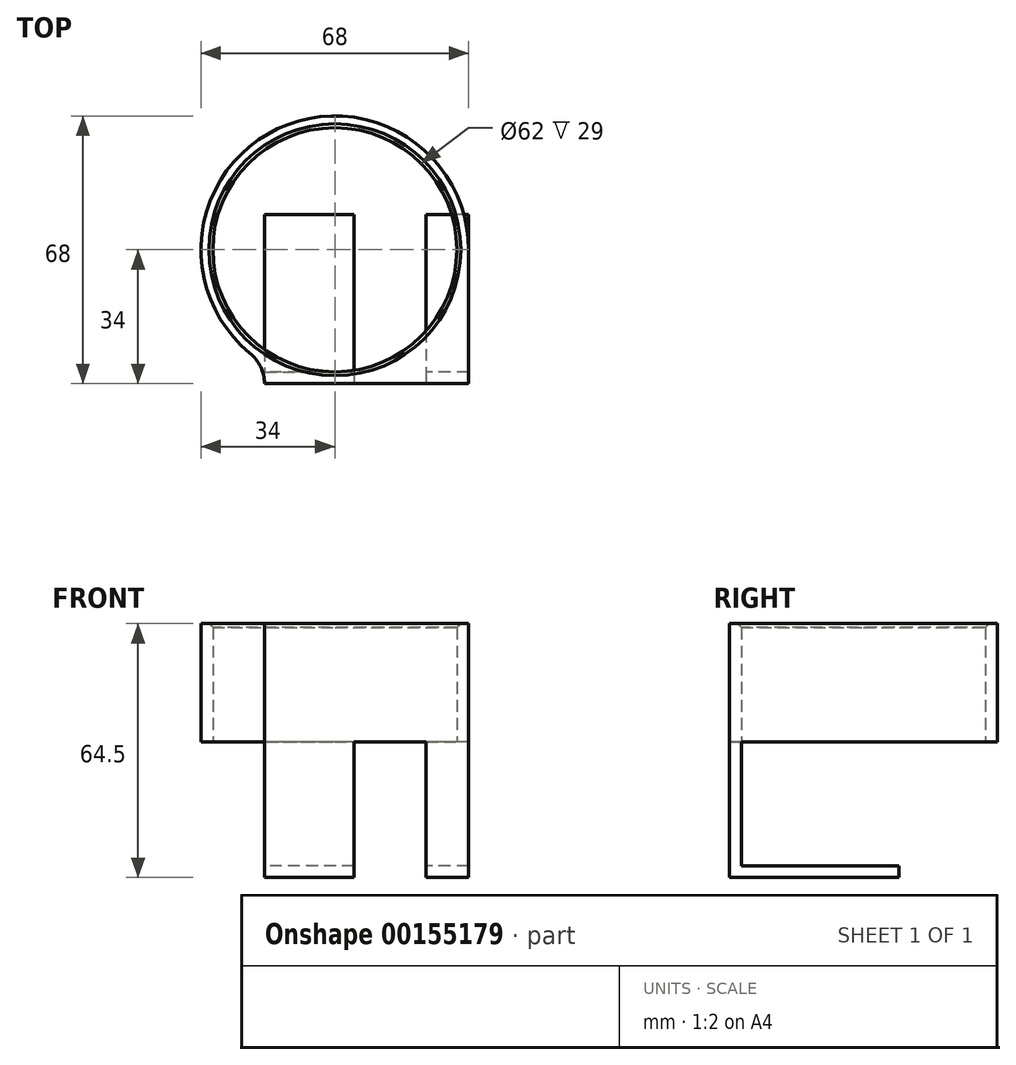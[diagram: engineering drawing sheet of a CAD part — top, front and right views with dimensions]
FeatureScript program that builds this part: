
annotation { "Feature Type Name" : "Feature", "Feature Type Description" : "" }
export const myFeature = defineFeature(function(context is Context, id is Id, definition is map)
    precondition{}
    {
        {
            var Q0;
            Q0=qCreatedBy(makeId("Top.planeOp"),FACE);
            var sketch = newSketch(context, id + "F0", { "sketchPlane" : qUnion([Q0])});
            skCircle(sketch, "E0", {"center": v(-34, 34) * mm, "radius": 31 * mm});
            skCircle(sketch, "E1.0", {"center": v(-34, 34) * mm, "radius": 34 * mm});
            skLineSegment(sketch, "E2", {"start": v(0, 0) * mm, "end": v(0, 49.7) * mm});
            skLineSegment(sketch, "E3", {"start": v(0, 0) * mm, "end": v(-51.85, 0) * mm});
            skLineSegment(sketch, "E4", {"start": v(-51.85, 0) * mm, "end": v(-51.85, 5.06) * mm});
            skSolve(sketch);
        }
        {
            var Q0;
            Q0=makeQuery(id+"F0.imprint","IMPRINT",FACE,{"disambiguationData":[TD([[makeQuery(id+"F0.imprint","IMPRINT",EDGE,{"derivedFrom":sQuery(id+"F0.wireOp",EDGE,"E0")}),-1.0]])]});
            var Q1;
            {var subQ0=sQuery(id+"F0.wireOp",EDGE,"E4");Q1=makeQuery(id+"F0.imprint","IMPRINT",FACE,{"disambiguationData":[TD([[makeQuery(id+"F0.imprint","IMPRINT",EDGE,{"derivedFrom":subQ0}),-1.0]])]});}
            var Q2;
            {var subQ0=sQuery(id+"F0.wireOp",EDGE,"E2");var subQ1=sQuery(id+"F0.wireOp",EDGE,"E1.0");var subQ2=makeQuery(id+"F0.imprint","INTERSECT",VERTEX,{"derivedFrom":[subQ1,subQ0]});Q2=makeQuery(id+"F0.imprint","IMPRINT",FACE,{"disambiguationData":[TD([[makeQuery(id+"F0.imprint","IMPRINT",EDGE,{"disambiguationData":[TD([[subQ2,1.0]])],"derivedFrom":subQ1}),-1.0]])]});}
            extrude(context, id + "F1", {"entities" : qUnion([Q0, Q1, Q2]), "depth" : 3 * mm});
        }
        {
            var Q0;
            Q0=makeQuery(id+"F1.opExtrude","CAP_FACE",FACE,{"disambiguationData":[OSD([sQuery(id+"F0.wireOp",EDGE,"E0"),sQuery(id+"F0.wireOp",EDGE,"E1.0"),sQuery(id+"F0.wireOp",EDGE,"E2"),sQuery(id+"F0.wireOp",EDGE,"E3"),sQuery(id+"F0.wireOp",EDGE,"E4")])],"isStart":true});
            var sketch = newSketch(context, id + "F2", { "sketchPlane" : qUnion([Q0])});
            skLineSegment(sketch, "E5", {"start": v(-51.85, 0) * mm, "end": v(-51.85, -3) * mm});
            skLineSegment(sketch, "E6", {"start": v(-51.85, -3) * mm, "end": v(-29.12, -3) * mm});
            skLineSegment(sketch, "E7", {"start": v(-29.12, -3) * mm, "end": v(-29.12, 0) * mm});
            skLineSegment(sketch, "E8", {"start": v(-29.12, 0) * mm, "end": v(-51.85, 0) * mm});
            skLineSegment(sketch, "E9", {"start": v(0, 0) * mm, "end": v(0, -3) * mm});
            skLineSegment(sketch, "E10", {"start": v(0, -3) * mm, "end": v(-10.82, -3) * mm});
            skLineSegment(sketch, "E11", {"start": v(-10.82, -3) * mm, "end": v(-10.82, 0) * mm});
            skLineSegment(sketch, "E12", {"start": v(-10.82, 0) * mm, "end": v(0, 0) * mm});
            skSolve(sketch);
        }
        {
            var Q0;
            Q0 = qSketchRegion(id + "F2", true);
            extrude(context, id + "F3", {"entities" : qUnion([Q0]), "operationType" : NewBodyOperationType.ADD, "depth" : 34.5 * mm});
        }
        {
            var Q0;
            Q0=makeQuery(id+"F3.opExtrude","SWEPT_FACE",FACE,{"disambiguationData":[OSD([sQuery(id+"F2.wireOp",EDGE,"E10")])]});
            var sketch = newSketch(context, id + "F4", { "sketchPlane" : qUnion([Q0])});
            skLineSegment(sketch, "E13.bottom", {"start": v(0, -34.5) * mm, "end": v(10.82, -34.5) * mm});
            skLineSegment(sketch, "E13.top", {"start": v(0, -31.5) * mm, "end": v(10.82, -31.5) * mm});
            skLineSegment(sketch, "E13.left", {"start": v(0, -34.5) * mm, "end": v(0, -31.5) * mm});
            skLineSegment(sketch, "E13.right", {"start": v(10.82, -34.5) * mm, "end": v(10.82, -31.5) * mm});
            skSolve(sketch);
        }
        {
            var Q0;
            Q0 = qSketchRegion(id + "F4", true);
            extrude(context, id + "F5", {"entities" : qUnion([Q0]), "operationType" : NewBodyOperationType.ADD, "depth" : 40 * mm});
        }
        {
            var Q0;
            Q0=makeQuery(id+"F3.opExtrude","SWEPT_FACE",FACE,{"disambiguationData":[OSD([sQuery(id+"F2.wireOp",EDGE,"E6")])]});
            var sketch = newSketch(context, id + "F6", { "sketchPlane" : qUnion([Q0])});
            skLineSegment(sketch, "E14.bottom", {"start": v(29.12, -34.5) * mm, "end": v(51.85, -34.5) * mm});
            skLineSegment(sketch, "E14.top", {"start": v(29.12, -31.5) * mm, "end": v(51.85, -31.5) * mm});
            skLineSegment(sketch, "E14.left", {"start": v(29.12, -34.5) * mm, "end": v(29.12, -31.5) * mm});
            skLineSegment(sketch, "E14.right", {"start": v(51.85, -34.5) * mm, "end": v(51.85, -31.5) * mm});
            skSolve(sketch);
        }
        {
            var Q0;
            Q0 = qSketchRegion(id + "F6", true);
            extrude(context, id + "F7", {"entities" : qUnion([Q0]), "operationType" : NewBodyOperationType.ADD, "depth" : 40 * mm});
        }
        {
            var Q0;
            Q0=makeQuery(id+"F1.opExtrude","CAP_FACE",FACE,{"disambiguationData":[OSD([sQuery(id+"F0.wireOp",EDGE,"E0"),sQuery(id+"F0.wireOp",EDGE,"E1.0"),sQuery(id+"F0.wireOp",EDGE,"E2"),sQuery(id+"F0.wireOp",EDGE,"E3"),sQuery(id+"F0.wireOp",EDGE,"E4")])],"isStart":false});
            extrude(context, id + "F8", {"entities" : qUnion([Q0]), "operationType" : NewBodyOperationType.ADD, "depth" : 27 * mm});
        }
        {
            var Q0;
            {var subQ0=sQuery(id+"F0.wireOp",EDGE,"E4");var subQ1=sQuery(id+"F0.wireOp",EDGE,"E1.0");Q0=makeQuery(id+"F8.boolean.opBoolean","MERGE",EDGE,{"derivedFrom":[makeQuery(id+"F1.opExtrude","SWEPT_EDGE",EDGE,{"disambiguationData":[OSD([subQ1,subQ0])]}),makeQuery(id+"F8.opExtrude","SWEPT_EDGE",EDGE,{"disambiguationData":[OSD([subQ1,subQ0])]})]});}
            fillet(context, id + "F9", {"entities" : qUnion([Q0]), "radius" : 10.33 * mm, "tangentPropagation" : true, "allowEdgeOverflow" : false});
        }
        {
            var Q0;
            Q0=makeQuery(id+"F8.opExtrude","CAP_EDGE",EDGE,{"disambiguationData":[OSD([sQuery(id+"F0.wireOp",EDGE,"E0")])],"isStart":false});
            chamfer(context, id + "F10", {"entities" : qUnion([Q0]), "width" : 1 * mm, "tangentPropagation" : true});
        }
    });
